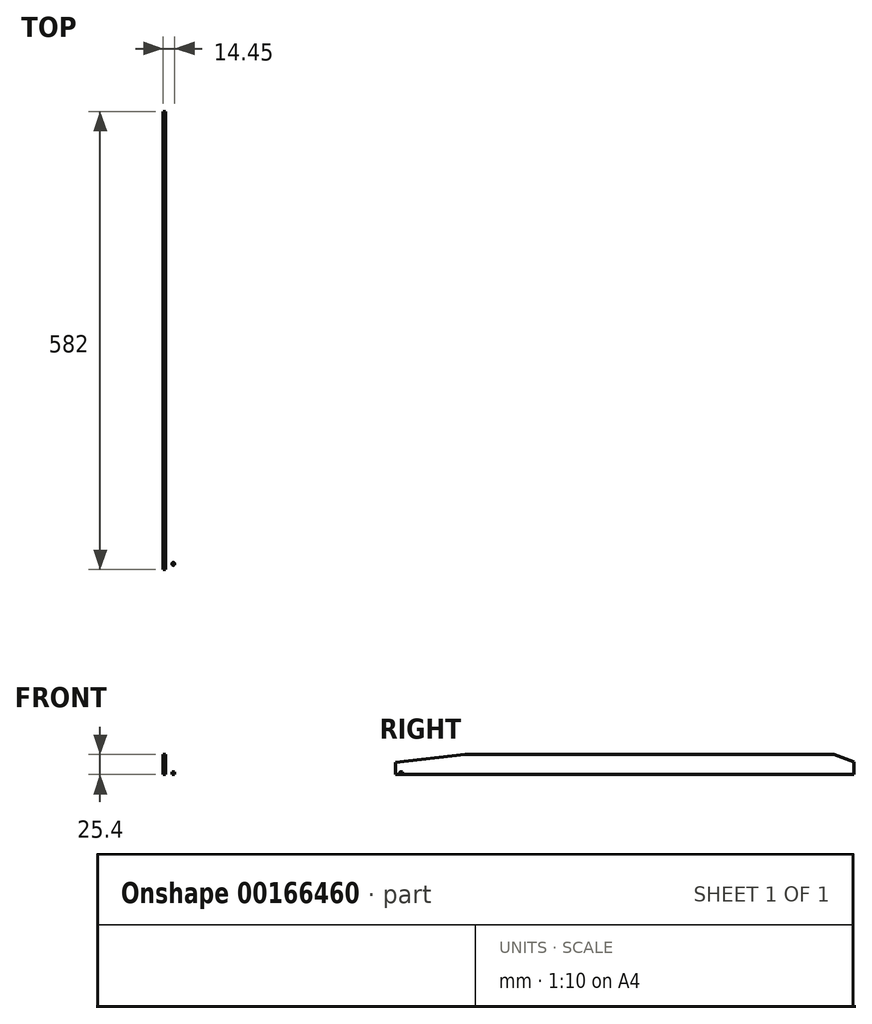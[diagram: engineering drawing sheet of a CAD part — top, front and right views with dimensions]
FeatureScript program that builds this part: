
annotation { "Feature Type Name" : "Feature", "Feature Type Description" : "" }
export const myFeature = defineFeature(function(context is Context, id is Id, definition is map)
    precondition{}
    {
        {
            var Q0;
            Q0=qCreatedBy(makeId("Front.planeOp"),FACE);
            var sketch = newSketch(context, id + "F0", { "sketchPlane" : qUnion([Q0])});
            skLineSegment(sketch, "E0.bottom", {"start": v(-12.7, 12.7) * mm, "end": v(-9.5, 12.7) * mm});
            skLineSegment(sketch, "E0.top", {"start": v(-12.7, -12.7) * mm, "end": v(12.7, -12.7) * mm});
            skLineSegment(sketch, "E0.left", {"start": v(-12.7, 12.7) * mm, "end": v(-12.7, -12.7) * mm});
            skLineSegment(sketch, "E0.right", {"start": v(12.7, -9.5) * mm, "end": v(12.7, -12.7) * mm});
            skPoint(sketch, "E0.middle", {"position": v(0, 0) * mm});
            skLineSegment(sketch, "E1", {"start": v(-9.5, 12.7) * mm, "end": v(-9.5, -9.5) * mm});
            skLineSegment(sketch, "E2", {"start": v(-9.5, -9.5) * mm, "end": v(12.7, -9.5) * mm});
            skPoint(sketch, "E3.orphan", {"position": v(12.7, 12.7) * mm});
            skSolve(sketch);
        }
        {
            var Q0;
            Q0=qSketchRegion(id+"F0",true);
            extrude(context, id + "F1", {"entities" : qUnion([Q0]), "endBound" : BoundingType.SYMMETRIC, "depth" : 582 * mm});
        }
        {
            var Q0;
            Q0=makeQuery(id+"F1.opExtrude","SWEPT_FACE",FACE,{"disambiguationData":[OSD([sQuery(id+"F0.wireOp",EDGE,"E0.top")])]});
            var sketch = newSketch(context, id + "F2", { "sketchPlane" : qUnion([Q0])});
            skPoint(sketch, "E4.middle", {"position": v(-12.7, 0) * mm});
            skCircle(sketch, "E5", {"center": v(-3.5, 77.5) * mm, "radius": 1.35 * mm});
            skCircle(sketch, "E6", {"center": v(-3.5, -77.5) * mm, "radius": 1.35 * mm});
            skCircle(sketch, "E7", {"center": v(-3.5, -202.5) * mm, "radius": 1.35 * mm});
            skLineSegment(sketch, "E8.bottom", {"start": v(-3.5, -279.49) * mm, "end": v(-12.7, -279.49) * mm, "construction": true});
            skLineSegment(sketch, "E8.left", {"start": v(-3.5, -279.49) * mm, "end": v(-3.5, 279.49) * mm, "construction": true});
            skCircle(sketch, "E9", {"center": v(-3.5, 202.5) * mm, "radius": 1.35 * mm});
            skLineSegment(sketch, "E10", {"start": v(-12.7, -279.49) * mm, "end": v(-12.7, 279.49) * mm, "construction": true});
            skPoint(sketch, "E8.top.end.orphan", {"position": v(-21.9, 279.49) * mm});
            skPoint(sketch, "E11.orphan", {"position": v(-21.9, -279.49) * mm});
            skLineSegment(sketch, "E12", {"start": v(-3.5, 279.49) * mm, "end": v(-12.7, 279.49) * mm, "construction": true});
            skSolve(sketch);
        }
        {
            var Q0;
            Q0=makeQuery(id+"F1.opExtrude","CAP_EDGE",EDGE,{"disambiguationData":[OSD([sQuery(id+"F0.wireOp",EDGE,"E0.bottom")])],"isStart":false});
            chamfer(context, id + "F3", {"entities" : qUnion([Q0]), "chamferType" : ChamferType.TWO_OFFSETS, "width1" : 88 * mm, "oppositeDirection" : false, "width2" : 10.1 * mm, "tangentPropagation" : true});
        }
        {
            var Q0;
            Q0=makeQuery(id+"F1.opExtrude","CAP_EDGE",EDGE,{"disambiguationData":[OSD([sQuery(id+"F0.wireOp",EDGE,"E0.bottom")])],"isStart":true});
            chamfer(context, id + "F4", {"entities" : qUnion([Q0]), "chamferType" : ChamferType.TWO_OFFSETS, "width1" : 9.5 * mm, "oppositeDirection" : false, "width2" : 25 * mm, "tangentPropagation" : true});
        }
        {
            var Q0;
            Q0=makeQuery(id+"F1.opExtrude","SWEPT_FACE",FACE,{"disambiguationData":[OSD([sQuery(id+"F0.wireOp",EDGE,"E2")])]});
            var sketch = newSketch(context, id + "F5", { "sketchPlane" : qUnion([Q0])});
            skCircle(sketch, "E13", {"center": v(0, 283.8) * mm, "radius": 1.75 * mm});
            skCircle(sketch, "E14.MirrorC", {"center": v(0, -283.8) * mm, "radius": 1.75 * mm});
            skSolve(sketch);
        }
        {
            var Q0;
            Q0=makeQuery(id+"F5.imprint","IMPRINT",FACE,{"disambiguationData":[TD([[makeQuery(id+"F5.imprint","IMPRINT",EDGE,{"derivedFrom":sQuery(id+"F5.wireOp",EDGE,"E14.MirrorC")}),-1.0]])]});
            var Q1;
            Q1=makeQuery(id+"F5.imprint","IMPRINT",FACE,{"disambiguationData":[TD([[makeQuery(id+"F5.imprint","IMPRINT",EDGE,{"derivedFrom":sQuery(id+"F5.wireOp",EDGE,"E13")}),1.0]])]});
            extrude(context, id + "F6", {"entities" : qUnion([Q0, Q1]), "operationType" : NewBodyOperationType.REMOVE, "endBound" : BoundingType.UP_TO_NEXT, "oppositeDirection" : true, "depth" : 25 * mm});
        }
        {
            var Q0;
            Q0 = qSketchRegion(id + "F2", true);
            extrude(context, id + "F7", {"entities" : qUnion([Q0]), "operationType" : NewBodyOperationType.REMOVE, "endBound" : BoundingType.THROUGH_ALL, "oppositeDirection" : true, "depth" : 25 * mm});
        }
    });
